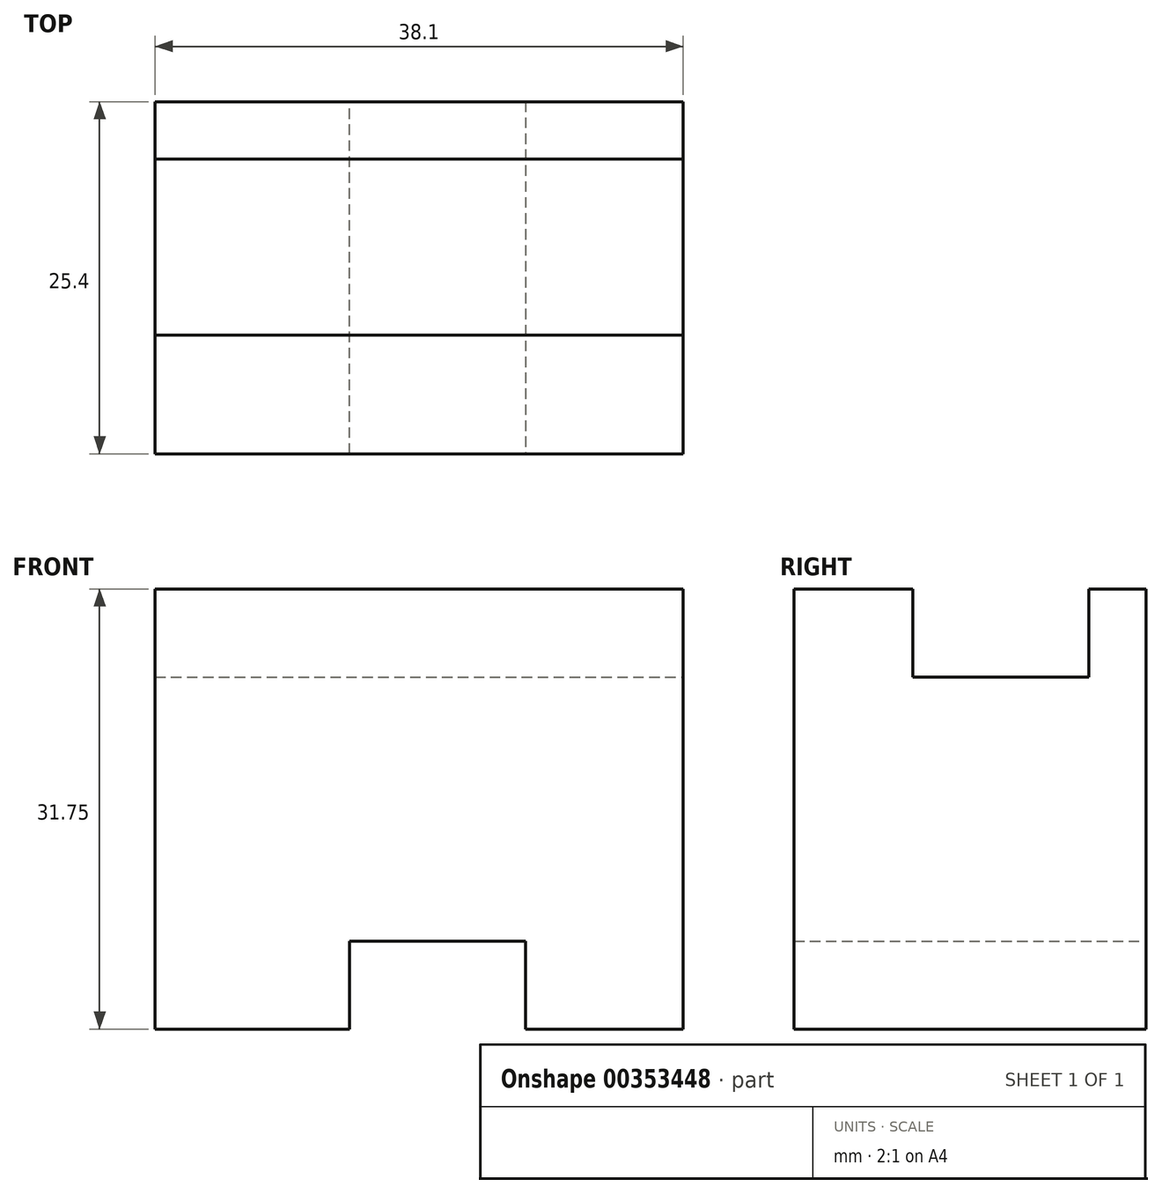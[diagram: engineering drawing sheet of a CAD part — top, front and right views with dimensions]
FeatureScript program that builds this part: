
annotation { "Feature Type Name" : "Feature", "Feature Type Description" : "" }
export const myFeature = defineFeature(function(context is Context, id is Id, definition is map)
    precondition{}
    {
        {
            var Q0;
            Q0=qCreatedBy(makeId("Right.planeOp"),FACE);
            var sketch = newSketch(context, id + "F0", { "sketchPlane" : qUnion([Q0])});
            skLineSegment(sketch, "E0.bottom", {"start": v(0, 0) * mm, "end": v(25.4, 0) * mm});
            skLineSegment(sketch, "E0.top", {"start": v(0, 31.75) * mm, "end": v(25.4, 31.75) * mm});
            skLineSegment(sketch, "E0.left", {"start": v(0, 0) * mm, "end": v(0, 31.75) * mm});
            skLineSegment(sketch, "E0.right", {"start": v(25.4, 0) * mm, "end": v(25.4, 31.75) * mm});
            skSolve(sketch);
        }
        {
            var Q0;
            Q0 = qSketchRegion(id + "F0", true);
            extrude(context, id + "F1", {"entities" : qUnion([Q0]), "depth" : 38.1 * mm});
        }
        {
            var Q0;
            Q0=makeQuery(id+"F1.opExtrude","SWEPT_FACE",FACE,{"disambiguationData":[OSD([sQuery(id+"F0.wireOp",EDGE,"E0.bottom")])]});
            var sketch = newSketch(context, id + "F2", { "sketchPlane" : qUnion([Q0])});
            skLineSegment(sketch, "E1", {"start": v(14.02, 0) * mm, "end": v(14.02, -25.4) * mm});
            skLineSegment(sketch, "E2", {"start": v(14.02, -25.4) * mm, "end": v(26.72, -25.4) * mm});
            skLineSegment(sketch, "E3", {"start": v(26.72, -25.4) * mm, "end": v(26.72, 0) * mm});
            skLineSegment(sketch, "E4", {"start": v(26.72, 0) * mm, "end": v(14.02, 0) * mm});
            skSolve(sketch);
        }
        {
            var Q0;
            Q0 = qSketchRegion(id + "F2", true);
            extrude(context, id + "F3", {"entities" : qUnion([Q0]), "operationType" : NewBodyOperationType.REMOVE, "oppositeDirection" : true, "depth" : 6.35 * mm});
        }
        {
            var Q0;
            Q0=makeQuery(id+"F1.opExtrude","SWEPT_FACE",FACE,{"disambiguationData":[OSD([sQuery(id+"F0.wireOp",EDGE,"E0.top")])]});
            var sketch = newSketch(context, id + "F4", { "sketchPlane" : qUnion([Q0])});
            skLineSegment(sketch, "E5", {"start": v(0, 21.27) * mm, "end": v(38.1, 21.27) * mm});
            skLineSegment(sketch, "E6", {"start": v(38.1, 21.27) * mm, "end": v(38.1, 8.57) * mm});
            skLineSegment(sketch, "E7", {"start": v(38.1, 8.57) * mm, "end": v(0, 8.57) * mm});
            skLineSegment(sketch, "E8", {"start": v(0, 8.57) * mm, "end": v(0, 21.27) * mm});
            skSolve(sketch);
        }
        {
            var Q0;
            Q0=makeQuery(id+"F4.imprint","IMPRINT",FACE,{"disambiguationData":[TD([[makeQuery(id+"F4.imprint","IMPRINT",EDGE,{"derivedFrom":sQuery(id+"F4.wireOp",EDGE,"E5")}),-1.0]])]});
            extrude(context, id + "F5", {"entities" : qUnion([Q0]), "operationType" : NewBodyOperationType.REMOVE, "oppositeDirection" : true, "depth" : 6.35 * mm});
        }
    });
